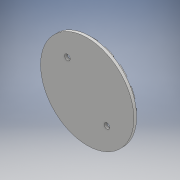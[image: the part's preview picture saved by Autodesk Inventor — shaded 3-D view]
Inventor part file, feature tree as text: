
AUTODESK INVENTOR PART (.ipt)
format: ipt  version: 2018 (Build 220112000, 112)  size: 163,328 bytes
history: native  units: mm
features: extrude x2, sketch x2, pattern_circular x1
ambient origin geometry x8: Origin, YZ Plane, XZ Plane, XY Plane, X Axis, Y Axis, Z Axis, Center Point
bodies: Solid1 (feature_tree)
feature tree (5):
  extrude  "Extrusion1"  Depth=15.0mm
  extrude  "Extrusion2"  Depth=3.0mm
  pattern_circular  "Circular Pattern1"  [2 undecoded]
  sketch  "Sketch1"  dims[d0=50.0mm d1=15.0mm]
  sketch  "Sketch2"  dims[d2=45.0deg d3=3.0mm d4=15.0mm d5=135.0deg d6=3.0mm d7=1.5mm d8=0.0mm d9=23.5mm d10=180.0deg d11=2.5mm d12=90.0deg d13=5.0mm d14=5.0mm d15=1.5mm d16=0.0mm d17=160.0mm d18=360.0deg]
note: 2 required parameter values undecoded (feature->parameter linkage not recoverable at this tier; creation-order binding heuristic only, values carry confidence <= 0.55)
